# Revit family: FT Secure Block_2020
name_source: partatom
category: Lighting Fixtures
units: mm (PartAtom-declared; Revit-internal decimal feet)

## family parameters
Always vertical = Yes
Cut with Voids When Loaded = No
Light Source = Yes
OmniClass Number = 23.80.70.00
OmniClass Title = Lighting
Part Type = Normal
Room Calculation Point = No
Round Connector Dimension = Use Diameter
Shared = No
Work Plane-Based = No

## types (6) — shared parameters
Color Filter = 16777215
Description = https://www.airfal.com
Dimming Lamp Color Temperature Shift = <None>
EX Area = Ex II 3GD Ex nR IIC T6 Gc Ex tc IIIC T85 ºC Dc
Emergency system = Yes
Emit from Line Length = 609.6 mm  [stored 2 ft]
Glow wire test = 960ºC
IK = IK10
IP = IP68-2
L = 415 mm  [stored 1.36155 ft]
Led Module = Yes
MacAdam Ellipse = 3/4
Photobiological risk group = RG1
Tilt Angle = 90.00°
URL = https://www.airfal.com
Unify glade rating = UGR<19
Useful life = L70B50>50000
Watts = 0 W
zero-valued in all types: Default Elevation

## per-type parameters (varying)
| type | Autonomy (h) | Mode | Photometric Web File |
| EXSB1 | 3 | Maintained | SECURE BLOCK 100lm.IES |
| EXSB4 | 3 | Non-maintained | SECURE BLOCK 100lm.IES |
| EXSB2 | 1.5 | Maintained | SECURE BLOCK 200lm.IES |
| EXSB5 | 1.5 | Non-maintained | SECURE BLOCK 200lm.IES |
| EXSB3 | 1 | Maintained | SECURE BLOCK 300lm.IES |
| EXSB6 | 1 | Non-maintained | SECURE BLOCK 300lm.IES |

note: [stored X ft] marks values corroborated as IEEE doubles in the binary element streams (Revit-internal decimal feet)

## geometry (parser evidence)
native form markers: Blend x8, Sweep x21
no freeform markers — native parametric forms only
